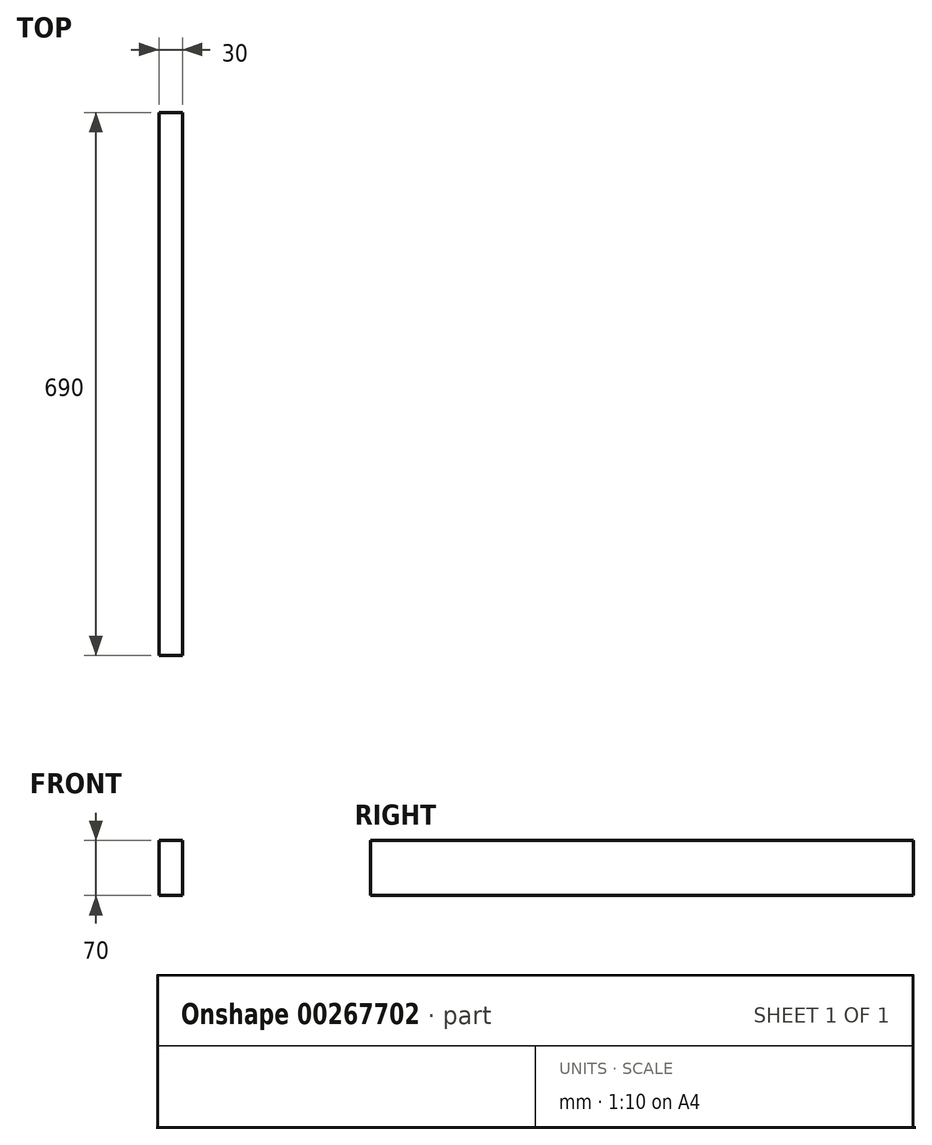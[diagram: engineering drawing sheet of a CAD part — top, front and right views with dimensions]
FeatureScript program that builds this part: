
annotation { "Feature Type Name" : "Feature", "Feature Type Description" : "" }
export const myFeature = defineFeature(function(context is Context, id is Id, definition is map)
    precondition{}
    {
        {
            var Q0;
            Q0=qCreatedBy(makeId("Front.planeOp"),FACE);
            var sketch = newSketch(context, id + "F0", { "sketchPlane" : qUnion([Q0])});
            skLineSegment(sketch, "E0.bottom", {"start": v(15, 35) * mm, "end": v(-15, 35) * mm});
            skLineSegment(sketch, "E0.top", {"start": v(15, -35) * mm, "end": v(-15, -35) * mm});
            skLineSegment(sketch, "E0.left", {"start": v(15, 35) * mm, "end": v(15, -35) * mm});
            skLineSegment(sketch, "E0.right", {"start": v(-15, 35) * mm, "end": v(-15, -35) * mm});
            skPoint(sketch, "E0.middle", {"position": v(0, 0) * mm});
            skSolve(sketch);
        }
        {
            var Q0;
            Q0 = qSketchRegion(id + "F0", true);
            extrude(context, id + "F1", {"entities" : qUnion([Q0]), "oppositeDirection" : true, "depth" : 690 * mm});
        }
    });
